# Revit family: Storage-Beam_Mounted-Teknion-JNBSF_Suspended_Credenza_Lateral_File-R2015
name_source: partatom
category: Furniture
revit_build: Autodesk Revit Architecture 2015 (Build: 20140323_1530(x64)
units: mm (PartAtom-declared; Revit-internal decimal feet)

## types (2) — shared parameters
Assembly Code = E2020200
Height = 24.125 "
Manufacturer = Teknion
Manufacturer Fax = 416.661.4586
Part Number = JNBSF
Product Documentation Link = https://www.teknion.com
Product Line = Cityline
Product Page URL = https://www.teknion.com
Series = Cityline
Sustainability Data = http://www.teknion.com
URL = www.teknion.com
Unit Weight URL = http://www.teknion.com
Warranty = http://www.teknion.com

## per-type parameters (varying)
| type | Case Front Thickness | Description | Front Finish | Metal-Cutout Offset | Model |
| Metal Front | 0.118 " | Suspended Credenza – Lateral File, Metal Front, Angled Structural Leg, 14" Case Height | Paint - Teknion - Foundation - Crisp Grey | 2 " | JNBSFMA14_ |
| Solid Front | 0.703 " | Suspended Credenza – Lateral File, Solid Front, Angled Structural Leg, 14" Case Height | Laminate - Teknion - 2T -Crisp Grey | 0.1 " | JNBSFSA14_ |

## geometry (parser evidence)
native form markers: Sweep x2
no freeform markers — native parametric forms only
